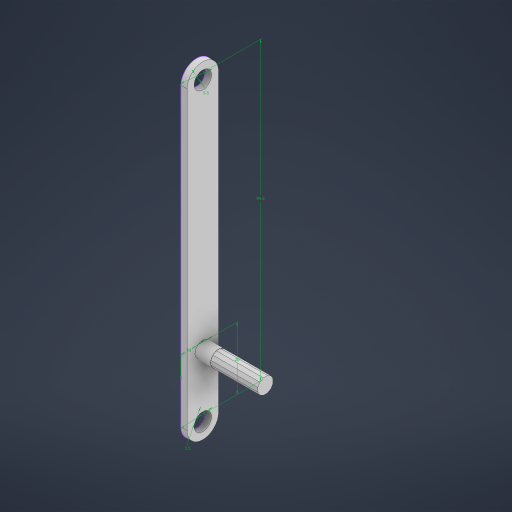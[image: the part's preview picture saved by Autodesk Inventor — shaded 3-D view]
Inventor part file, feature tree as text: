
AUTODESK INVENTOR PART (.ipt)
format: ipt  version: 2024 (Build 280153000, 153)  size: 220,672 bytes
history: native  units: mm
features: extrude x3, other x1, sketch x1
ambient origin geometry x8: Origin, YZ Plane, XZ Plane, XY Plane, X Axis, Y Axis, Z Axis, Center Point
bodies: Body1 (feature_tree)
feature tree (5):
  other  "솔리드1"
  sketch  "스케치1"
  extrude  "돌출1"  Depth=5.0mm
  extrude  "돌출2"  Depth=10.0mm
  extrude  "돌출3"  Depth=10.0mm
